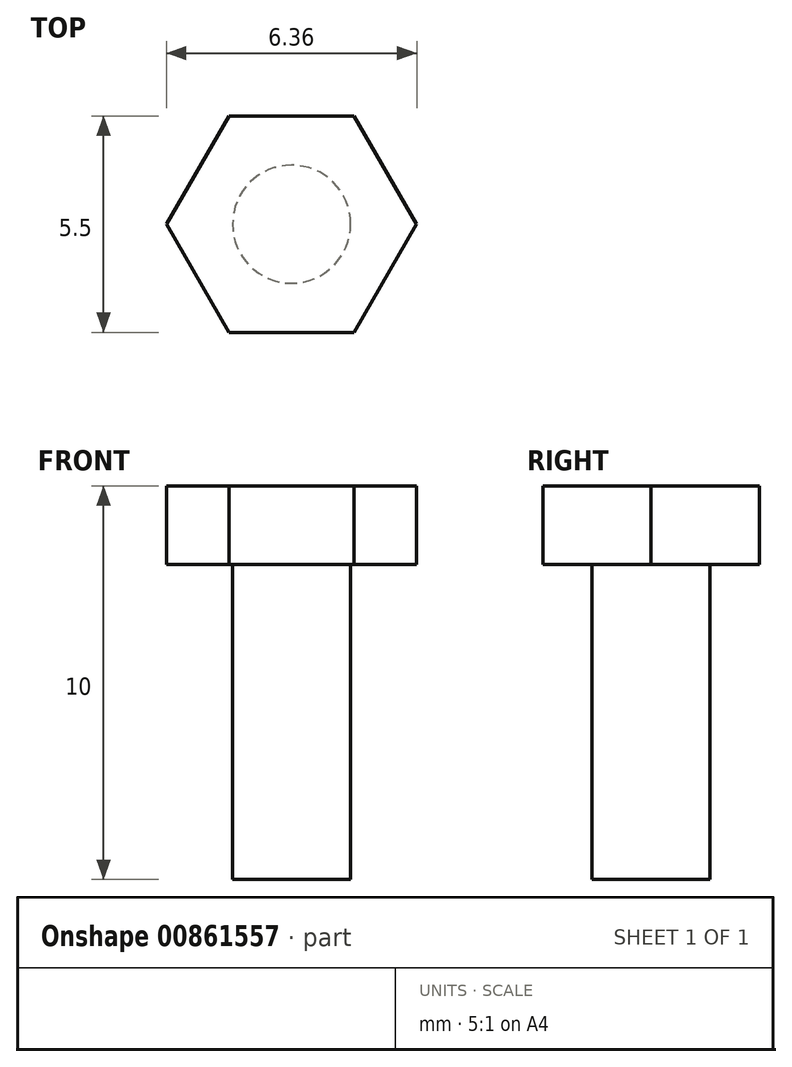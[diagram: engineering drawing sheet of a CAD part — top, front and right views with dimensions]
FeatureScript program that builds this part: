
annotation { "Feature Type Name" : "Feature", "Feature Type Description" : "" }
export const myFeature = defineFeature(function(context is Context, id is Id, definition is map)
    precondition{}
    {
        {
            var Q0;
            Q0=qCreatedBy(makeId("Top.planeOp"),FACE);
            var sketch = newSketch(context, id + "F0", { "sketchPlane" : qUnion([Q0])});
            skCircle(sketch, "E0.cCircle", {"center": v(0, 0) * mm, "radius": 2.75 * mm, "construction": true});
            skLineSegment(sketch, "E0.0", {"start": v(1.59, 2.75) * mm, "end": v(3.18, 0) * mm});
            skLineSegment(sketch, "E0.1", {"start": v(3.18, 0) * mm, "end": v(1.59, -2.75) * mm});
            skLineSegment(sketch, "E0.2", {"start": v(1.59, -2.75) * mm, "end": v(-1.59, -2.75) * mm});
            skLineSegment(sketch, "E0.3", {"start": v(-1.59, -2.75) * mm, "end": v(-3.18, 0) * mm});
            skLineSegment(sketch, "E0.4", {"start": v(-3.18, 0) * mm, "end": v(-1.59, 2.75) * mm});
            skLineSegment(sketch, "E0.5", {"start": v(-1.59, 2.75) * mm, "end": v(1.59, 2.75) * mm});
            skPoint(sketch, "E0.0.midPoint", {"position": v(2.38, 1.38) * mm});
            skSolve(sketch);
        }
        {
            var Q0;
            Q0 = qSketchRegion(id + "F0", true);
            extrude(context, id + "F1", {"entities" : qUnion([Q0]), "depth" : 2 * mm, "offsetDistance" : 25 * mm});
        }
        {
            var Q0;
            Q0=makeQuery(id+"F1.opExtrude","CAP_FACE",FACE,{"disambiguationData":[OSD([sQuery(id+"F0.wireOp",EDGE,"E0.0"),sQuery(id+"F0.wireOp",EDGE,"E0.1"),sQuery(id+"F0.wireOp",EDGE,"E0.2"),sQuery(id+"F0.wireOp",EDGE,"E0.3"),sQuery(id+"F0.wireOp",EDGE,"E0.4"),sQuery(id+"F0.wireOp",EDGE,"E0.5")])],"isStart":true});
            var sketch = newSketch(context, id + "F2", { "sketchPlane" : qUnion([Q0])});
            skCircle(sketch, "E1", {"center": v(0, 0) * mm, "radius": 1.5 * mm});
            skSolve(sketch);
        }
        {
            var Q0;
            Q0 = qSketchRegion(id + "F2", true);
            extrude(context, id + "F3", {"entities" : qUnion([Q0]), "operationType" : NewBodyOperationType.ADD, "depth" : 8 * mm, "offsetDistance" : 25 * mm});
        }
        {
            var Q0;
            Q0=makeQuery(id+"F1.opExtrude","SWEPT_BODY",BODY,{"disambiguationData":[OSD([sQuery(id+"F0.wireOp",EDGE,"E0.0"),sQuery(id+"F0.wireOp",EDGE,"E0.1"),sQuery(id+"F0.wireOp",EDGE,"E0.2"),sQuery(id+"F0.wireOp",EDGE,"E0.3"),sQuery(id+"F0.wireOp",EDGE,"E0.4"),sQuery(id+"F0.wireOp",EDGE,"E0.5")])]});
            transform(context, id + "F4", {"entities" : qUnion([Q0]), "transformType" : TransformType.TRANSLATION_3D, "dx" : 0 * mm, "dy" : 0 * mm, "dz" : 0 * mm, "makeCopy" : true});
        }
    });
